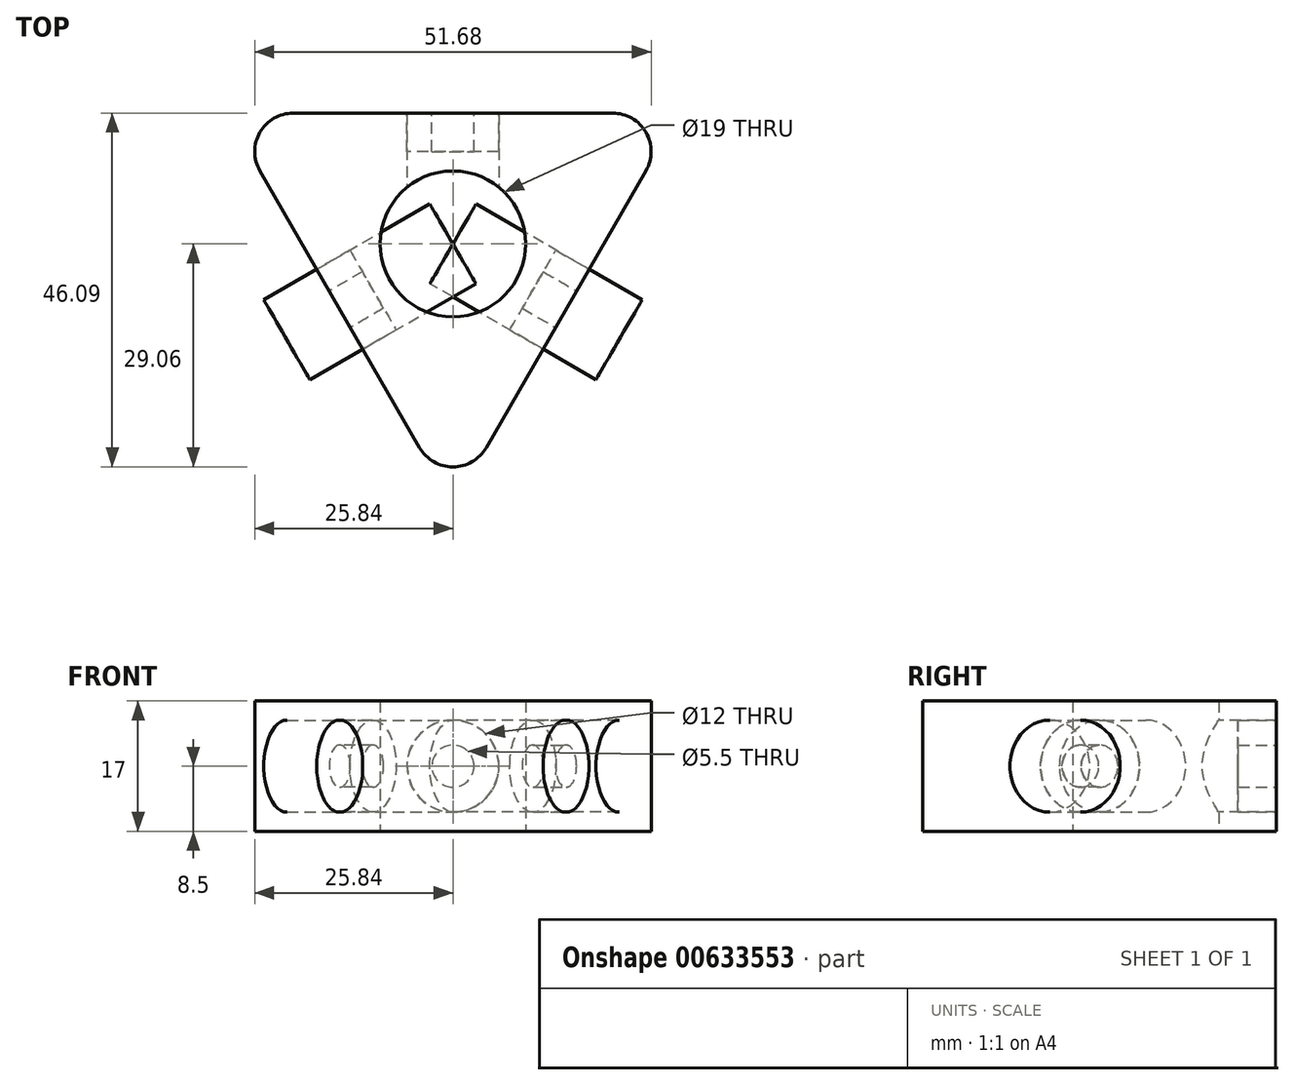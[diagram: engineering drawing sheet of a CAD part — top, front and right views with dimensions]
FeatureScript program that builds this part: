
annotation { "Feature Type Name" : "Feature", "Feature Type Description" : "" }
export const myFeature = defineFeature(function(context is Context, id is Id, definition is map)
    precondition{}
    {
        {
            var Q0;
            Q0=qCreatedBy(makeId("Top.planeOp"),FACE);
            var sketch = newSketch(context, id + "F0", { "sketchPlane" : qUnion([Q0])});
            skLineSegment(sketch, "E0", {"start": v(-29.5, 17.03) * mm, "end": v(29.5, 17.03) * mm, "construction": true});
            skLineSegment(sketch, "E1", {"start": v(25.17, 9.53) * mm, "end": v(4.33, -26.56) * mm});
            skLineSegment(sketch, "E2", {"start": v(-4.33, -26.56) * mm, "end": v(-25.17, 9.53) * mm});
            skCircle(sketch, "E3", {"center": v(0, 0) * mm, "radius": 34.06 * mm, "construction": true});
            skCircle(sketch, "E4", {"center": v(0, 0) * mm, "radius": 9.5 * mm});
            skLineSegment(sketch, "E5", {"start": v(0, 0) * mm, "end": v(29.5, 17.03) * mm, "construction": true});
            skLineSegment(sketch, "E6.MirrorCS", {"start": v(20.84, 17.03) * mm, "end": v(-20.84, 17.03) * mm});
            skPoint(sketch, "E7.visualSharp", {"position": v(-29.5, 17.03) * mm});
            skArc(sketch, "E7.filletArc", {"start": v(-20.84, 17.03) * mm, "mid": v(-25.17, 14.53) * mm, "end": v(-25.17, 9.53) * mm});
            skPoint(sketch, "E8.visualSharp", {"position": v(29.5, 17.03) * mm});
            skArc(sketch, "E8.filletArc", {"start": v(25.17, 9.53) * mm, "mid": v(25.17, 14.53) * mm, "end": v(20.84, 17.03) * mm});
            skPoint(sketch, "E9.visualSharp", {"position": v(0, -34.06) * mm});
            skArc(sketch, "E9.filletArc", {"start": v(-4.33, -26.56) * mm, "mid": v(0, -29.06) * mm, "end": v(4.33, -26.56) * mm});
            skLineSegment(sketch, "E10", {"start": v(-29.5, 17.03) * mm, "end": v(0, -34.06) * mm, "construction": true});
            skLineSegment(sketch, "E11", {"start": v(0, -34.06) * mm, "end": v(29.5, 17.03) * mm, "construction": true});
            skSolve(sketch);
        }
        {
            var Q0;
            Q0=makeQuery(id+"F0.imprint","IMPRINT",FACE,{"disambiguationData":[TD([[makeQuery(id+"F0.imprint","IMPRINT",EDGE,{"derivedFrom":sQuery(id+"F0.wireOp",EDGE,"E4")}),-1.0]])]});
            extrude(context, id + "F1", {"entities" : qUnion([Q0]), "endBound" : BoundingType.SYMMETRIC, "depth" : 17 * mm, "offsetDistance" : 25 * mm});
        }
        {
            var Q0;
            Q0=qCreatedBy(makeId("Front.planeOp"),FACE);
            var sketch = newSketch(context, id + "F2", { "sketchPlane" : qUnion([Q0])});
            skCircle(sketch, "E12", {"center": v(0, 0) * mm, "radius": 6 * mm});
            skSolve(sketch);
        }
        {
            var Q0;
            Q0=qSketchRegion(id+"F2",true);
            extrude(context, id + "F3", {"entities" : qUnion([Q0]), "oppositeDirection" : true, "depth" : 25 * mm, "offsetDistance" : 25 * mm});
        }
        {
            var Q0;
            Q0=makeQuery(id+"F3.opExtrude","SWEPT_BODY",BODY,{"disambiguationData":[OSD([sQuery(id+"F2.wireOp",EDGE,"E12")])]});
            var Q1;
            Q1=sQuery(id+"F0.wireOp",EDGE,"E4");
            circularPattern(context, id + "F4", {"entities" : qUnion([Q0]), "axis" : qUnion([Q1]), "angle" : 360 * degree, "instanceCount" : 3, "equalSpace" : true});
        }
        {
            var Q0;
            Q0=makeQuery(id+"F3.opExtrude","SWEPT_BODY",BODY,{"disambiguationData":[OSD([sQuery(id+"F2.wireOp",EDGE,"E12")])]});
            var Q1;
            Q1=makeQuery(id+"F1.opExtrude","SWEPT_BODY",BODY,{"disambiguationData":[OSD([sQuery(id+"F0.wireOp",EDGE,"8567cb31-eef4-4487-9e7d-64f7d120fd18.0"),sQuery(id+"F0.wireOp",EDGE,"8567cb31-eef4-4487-9e7d-64f7d120fd18.1"),sQuery(id+"F0.wireOp",EDGE,"8567cb31-eef4-4487-9e7d-64f7d120fd18.2"),sQuery(id+"F0.wireOp",EDGE,"99e7613c-3a71-48ef-a2ed-1ba2aef9368b.filletArc"),sQuery(id+"F0.wireOp",EDGE,"cfcb64ef-2180-43a3-8ec9-52d5588a1f2f.filletArc"),sQuery(id+"F0.wireOp",EDGE,"6011dbe8-f45c-4d00-b308-e3a8662c87ca.filletArc"),sQuery(id+"F0.wireOp",EDGE,"E4")])]});
            booleanBodies(context, id + "F5", {"operationType" : BooleanOperationType.SUBTRACTION, "tools" : qUnion([Q0]), "targets" : qUnion([Q1])});
        }
        {
            var Q0;
            Q0=makeQuery(id+"F1.opExtrude","SWEPT_FACE",FACE,{"disambiguationData":[OSD([sQuery(id+"F0.wireOp",EDGE,"E6.MirrorCS")])]});
            var sketch = newSketch(context, id + "F6", { "sketchPlane" : qUnion([Q0])});
            skCircle(sketch, "E13", {"center": v(0, 0) * mm, "radius": 6 * mm});
            skCircle(sketch, "E14", {"center": v(0, 0) * mm, "radius": 2.75 * mm});
            skSolve(sketch);
        }
        {
            var Q0;
            Q0=makeQuery(id+"F6.imprint","IMPRINT",FACE,{"disambiguationData":[TD([[makeQuery(id+"F6.imprint","IMPRINT",EDGE,{"derivedFrom":sQuery(id+"F6.wireOp",EDGE,"E13")}),-1.0]])]});
            extrude(context, id + "F7", {"entities" : qUnion([Q0]), "oppositeDirection" : true, "depth" : 5 * mm, "offsetDistance" : 25 * mm});
        }
        {
            var Q0;
            Q0=makeQuery(id+"F7.opExtrude","SWEPT_BODY",BODY,{"disambiguationData":[OSD([sQuery(id+"F6.wireOp",EDGE,"E13"),sQuery(id+"F6.wireOp",EDGE,"E14")])]});
            var Q1;
            Q1=makeQuery(id+"F1.opExtrude","CAP_EDGE",EDGE,{"disambiguationData":[OSD([sQuery(id+"F0.wireOp",EDGE,"E4")])],"isStart":false});
            circularPattern(context, id + "F8", {"entities" : qUnion([Q0]), "axis" : qUnion([Q1]), "angle" : 360 * degree, "instanceCount" : 3, "equalSpace" : true});
        }
    });
